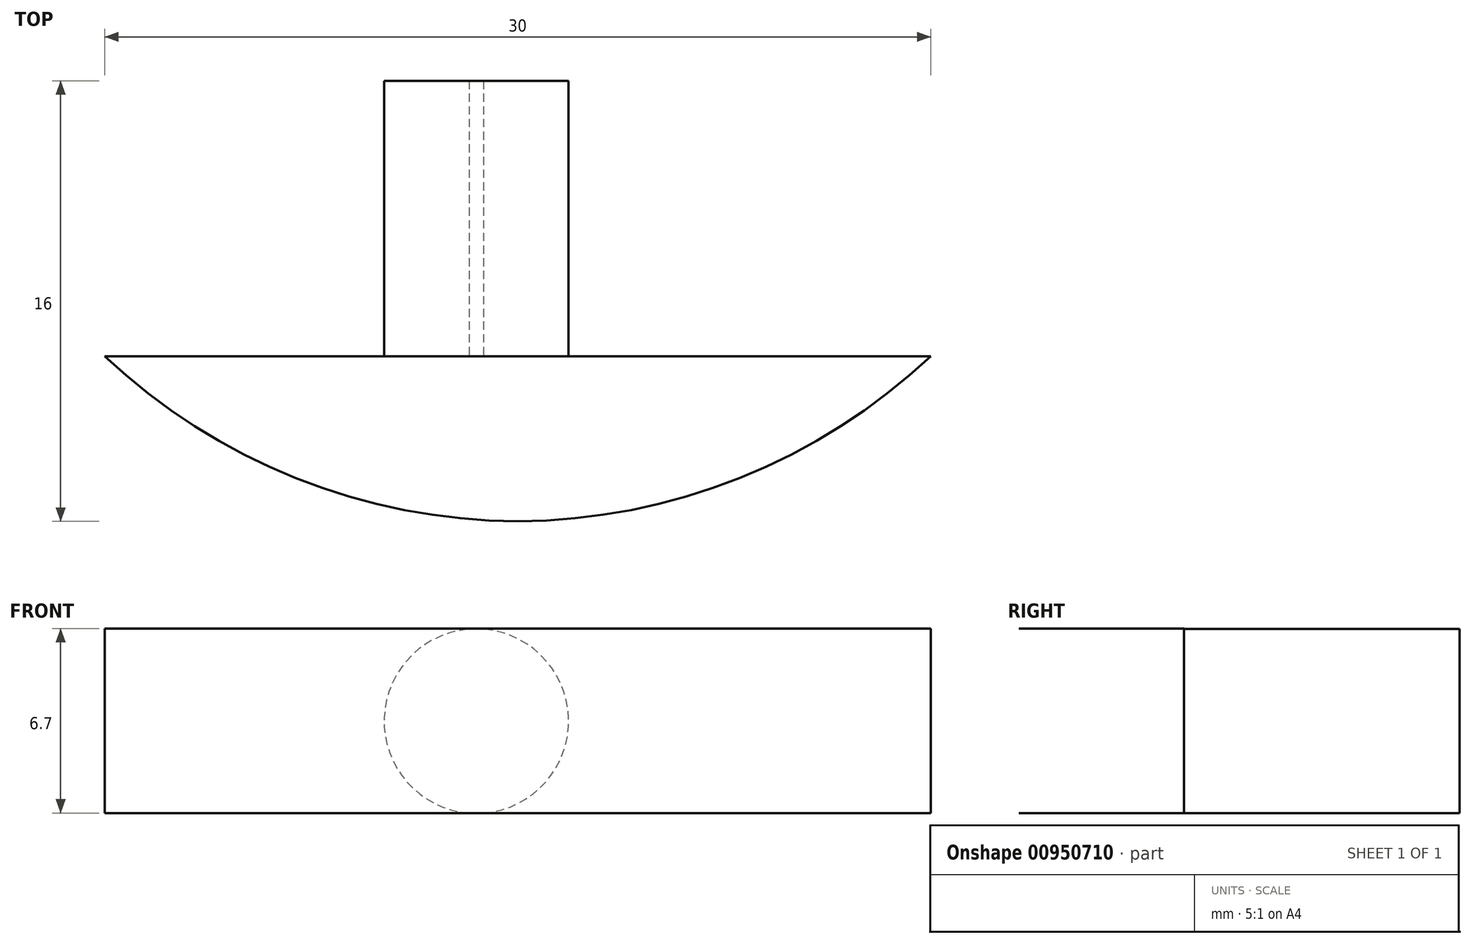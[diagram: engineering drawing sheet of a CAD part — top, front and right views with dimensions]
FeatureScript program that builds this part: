
annotation { "Feature Type Name" : "Feature", "Feature Type Description" : "" }
export const myFeature = defineFeature(function(context is Context, id is Id, definition is map)
    precondition{}
    {
        {
            var Q0;
            Q0=qCreatedBy(makeId("Front.planeOp"),FACE);
            var sketch = newSketch(context, id + "F0", { "sketchPlane" : qUnion([Q0])});
            skLineSegment(sketch, "E0.bottom", {"start": v(-19.44, 15.98) * mm, "end": v(10.56, 15.98) * mm});
            skLineSegment(sketch, "E0.top", {"start": v(-19.44, 9.28) * mm, "end": v(10.56, 9.28) * mm});
            skLineSegment(sketch, "E0.left", {"start": v(-19.44, 15.98) * mm, "end": v(-19.44, 9.28) * mm});
            skLineSegment(sketch, "E0.right", {"start": v(10.56, 15.98) * mm, "end": v(10.56, 9.28) * mm});
            skCircle(sketch, "E1", {"center": v(-5.94, 12.62) * mm, "radius": 3.35 * mm});
            skSolve(sketch);
        }
        {
            var Q0;
            Q0=makeQuery(id+"F0.imprint","IMPRINT",FACE,{"disambiguationData":[TD([[makeQuery(id+"F0.imprint","IMPRINT",EDGE,{"derivedFrom":sQuery(id+"F0.wireOp",EDGE,"E0.bottom")}),-1.0]])]});
            var Q1;
            {var subQ0=sQuery(id+"F0.wireOp",EDGE,"E1");var subQ1=sQuery(id+"F0.wireOp",EDGE,"E0.top");var subQ2=makeQuery(id+"F0.imprint","INTERSECT",VERTEX,{"disambiguationData":[OD(0.0)],"derivedFrom":[subQ1,subQ0]});Q1=makeQuery(id+"F0.imprint","IMPRINT",FACE,{"disambiguationData":[TD([[makeQuery(id+"F0.imprint","IMPRINT",EDGE,{"disambiguationData":[TD([[subQ2,-1.0]])],"derivedFrom":subQ1}),1.0]])]});}
            extrude(context, id + "F1", {"entities" : qUnion([Q0, Q1]), "depth" : 6 * mm, "offsetDistance" : 25 * mm});
        }
        {
            var Q0;
            {var subQ0=sQuery(id+"F0.wireOp",EDGE,"E1");var subQ1=sQuery(id+"F0.wireOp",EDGE,"E0.top");var subQ2=makeQuery(id+"F0.imprint","INTERSECT",VERTEX,{"disambiguationData":[OD(0.0)],"derivedFrom":[subQ1,subQ0]});Q0=makeQuery(id+"F0.imprint","IMPRINT",FACE,{"disambiguationData":[TD([[makeQuery(id+"F0.imprint","IMPRINT",EDGE,{"disambiguationData":[TD([[subQ2,-1.0]])],"derivedFrom":subQ1}),1.0]])]});}
            extrude(context, id + "F2", {"entities" : qUnion([Q0]), "operationType" : NewBodyOperationType.ADD, "oppositeDirection" : true, "depth" : 10 * mm, "offsetDistance" : 25 * mm});
        }
        {
            var Q0;
            Q0=makeQuery(id+"F1.opExtrude","CAP_EDGE",EDGE,{"disambiguationData":[OSD([sQuery(id+"F0.wireOp",EDGE,"E0.left")])],"isStart":false});
            var Q1;
            Q1=makeQuery(id+"F1.opExtrude","CAP_EDGE",EDGE,{"disambiguationData":[OSD([sQuery(id+"F0.wireOp",EDGE,"E0.right")])],"isStart":false});
            fillet(context, id + "F3", {"entities" : qUnion([Q0, Q1]), "radius" : 22 * mm, "tangentPropagation" : true, "allowEdgeOverflow" : false});
        }
    });
